# Revit family: Dachhalter Big Foot 450 Vlies
name_source: partatom
category: HLS-Bauteile
units: mm (PartAtom-declared; Revit-internal decimal feet)

## family parameters
Arbeitsebenenbasiert = Ja
Beim Laden mit Abzugskörper schneiden = Nein
Bemaßung runder Anschluss = Durchmesser verwenden
Beschriftungsausrichtung beibehalten = Nein
Gemeinsam genutzt = Ja
Immer vertikal = Nein
Klassifizierung = Keine
Raumberechnungspunkt = Nein
Teiletyp = Normal

## types (1)
- Dachhalter Big Foot 450 Vlies
    Artikelnummer = 08197613
    Breite = 492 mm  [stored 1.61417 ft]
    EAN = 4250928455598
    Fabrikat = MEFA
    Farbe = Schwarz
    Gewicht = 0,06 kg
    Gewicht pro Bauteil = 0,06 kg
    Kurztext1 = Trennvlies BIG FOOT® 450
    Kurztext2 = 492 x 492 x 3,5 mm Polyester
    Länge = 492 mm  [stored 1.61417 ft]
    Material = Kunststoff
    Materialname = Polyester
    Mengeneinheit = St
    Stärke = 4 mm  [stored 0.0131234 ft]
    Vorgabe-Ansicht = 1219 mm
    vpe = 1

note: [stored X ft] marks values corroborated as IEEE doubles in the binary element streams (Revit-internal decimal feet)
